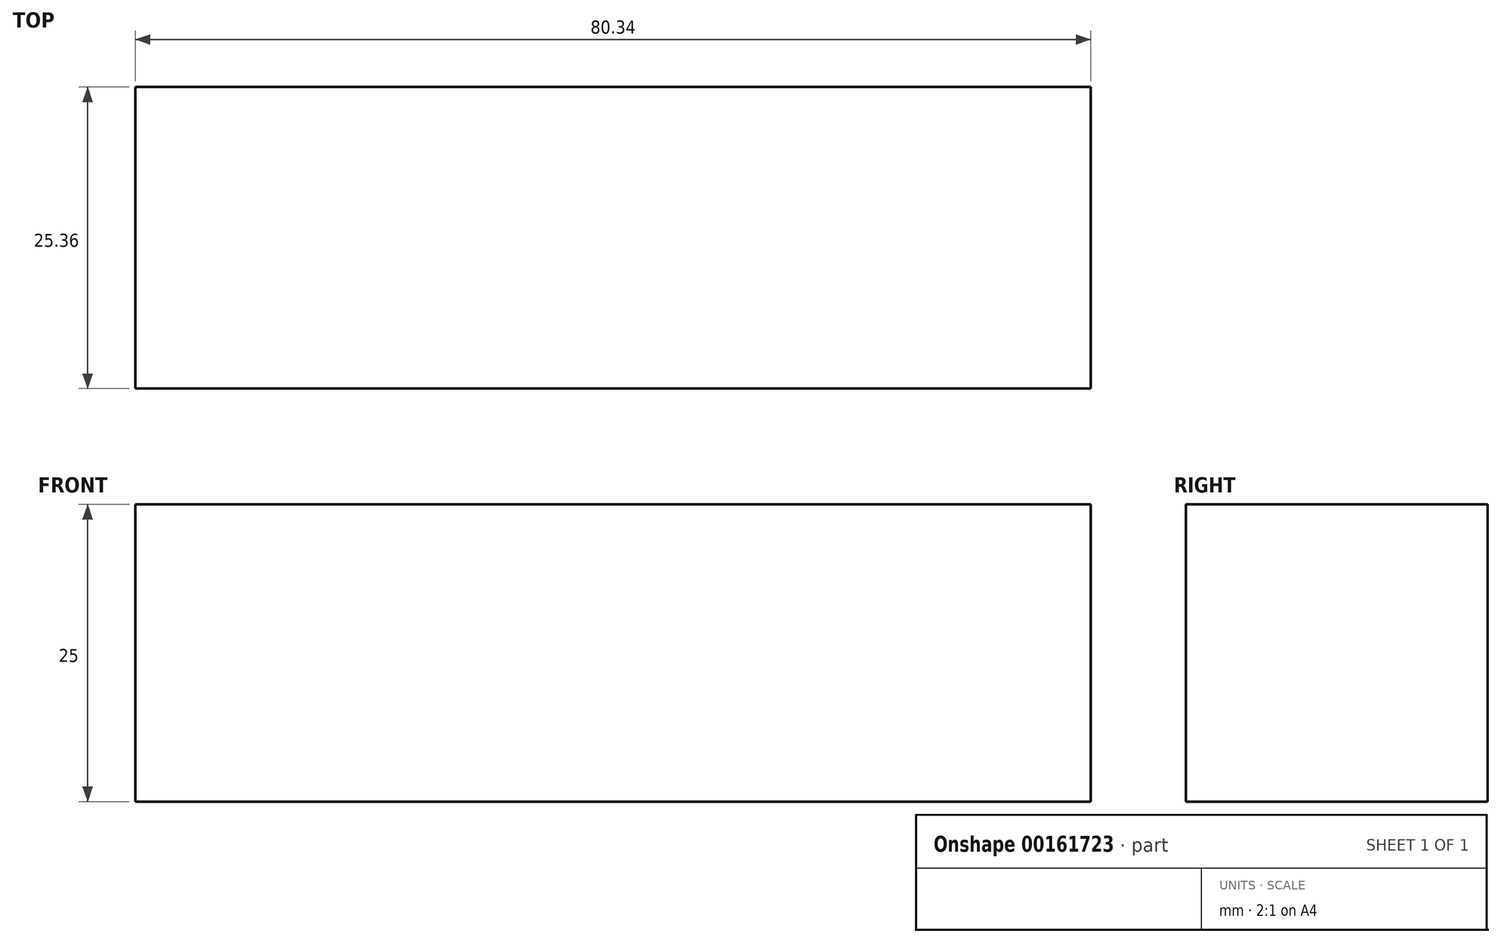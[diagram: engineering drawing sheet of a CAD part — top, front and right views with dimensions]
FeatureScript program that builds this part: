
annotation { "Feature Type Name" : "Feature", "Feature Type Description" : "" }
export const myFeature = defineFeature(function(context is Context, id is Id, definition is map)
    precondition{}
    {
        {
            var Q0;
            Q0=qCreatedBy(makeId("Top.planeOp"),FACE);
            var sketch = newSketch(context, id + "F0", { "sketchPlane" : qUnion([Q0])});
            skLineSegment(sketch, "E0.bottom", {"start": v(-48.2, 0) * mm, "end": v(32.14, 0) * mm});
            skLineSegment(sketch, "E0.top", {"start": v(-48.2, -25.36) * mm, "end": v(32.14, -25.36) * mm});
            skLineSegment(sketch, "E0.left", {"start": v(-48.2, 0) * mm, "end": v(-48.2, -25.36) * mm});
            skLineSegment(sketch, "E0.right", {"start": v(32.14, 0) * mm, "end": v(32.14, -25.36) * mm});
            skSolve(sketch);
        }
        {
            var Q0;
            Q0 = qSketchRegion(id + "F0", true);
            extrude(context, id + "F1", {"entities" : qUnion([Q0]), "depth" : 25 * mm});
        }
    });
